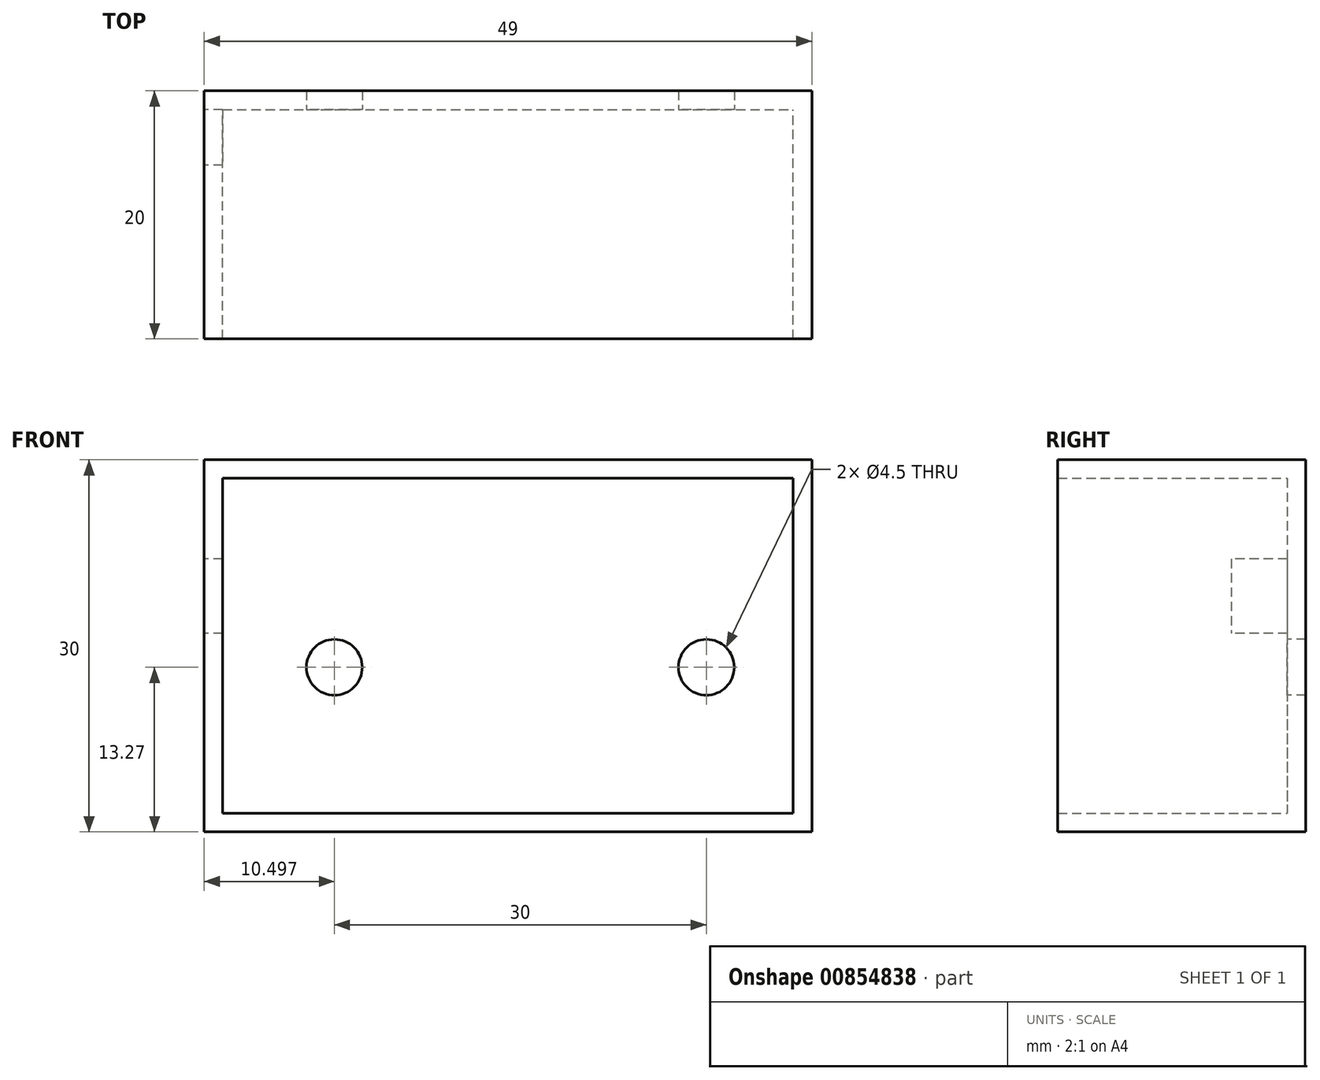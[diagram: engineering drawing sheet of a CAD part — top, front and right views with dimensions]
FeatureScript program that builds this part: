
annotation { "Feature Type Name" : "Feature", "Feature Type Description" : "" }
export const myFeature = defineFeature(function(context is Context, id is Id, definition is map)
    precondition{}
    {
        {
            var Q0;
            Q0=qCreatedBy(makeId("Front.planeOp"),FACE);
            var sketch = newSketch(context, id + "F0", { "sketchPlane" : qUnion([Q0])});
            skLineSegment(sketch, "E0.bottom", {"start": v(-23.27, 16.73) * mm, "end": v(25.73, 16.73) * mm});
            skLineSegment(sketch, "E0.top", {"start": v(-23.27, -13.27) * mm, "end": v(25.73, -13.27) * mm});
            skLineSegment(sketch, "E0.left", {"start": v(-23.27, 16.73) * mm, "end": v(-23.27, -13.27) * mm});
            skLineSegment(sketch, "E0.right", {"start": v(25.73, 16.73) * mm, "end": v(25.73, -13.27) * mm});
            skSolve(sketch);
        }
        {
            var Q0;
            Q0=makeQuery(id+"F0.imprint","IMPRINT",FACE,{"disambiguationData":[TD([[makeQuery(id+"F0.imprint","IMPRINT",EDGE,{"derivedFrom":sQuery(id+"F0.wireOp",EDGE,"E0.bottom")}),-1.0]])]});
            extrude(context, id + "F1", {"entities" : qUnion([Q0]), "depth" : 20 * mm, "offsetDistance" : 25 * mm});
        }
        {
            var Q0;
            Q0=makeQuery(id+"F1.opExtrude","CAP_FACE",FACE,{"disambiguationData":[OSD([sQuery(id+"F0.wireOp",EDGE,"E0.bottom"),sQuery(id+"F0.wireOp",EDGE,"E0.top"),sQuery(id+"F0.wireOp",EDGE,"E0.left"),sQuery(id+"F0.wireOp",EDGE,"E0.right")])],"isStart":false});
            shell(context, id + "F2", {"entities" : qUnion([Q0]), "thickness" : 1.5 * mm});
        }
        {
            var Q0;
            Q0=makeQuery(id+"F2.opShell","OFFSET_FACE",FACE,{"disambiguationData":[OSD([sQuery(id+"F0.wireOp",EDGE,"E0.bottom"),sQuery(id+"F0.wireOp",EDGE,"E0.top"),sQuery(id+"F0.wireOp",EDGE,"E0.left"),sQuery(id+"F0.wireOp",EDGE,"E0.right")])]});
            var sketch = newSketch(context, id + "F3", { "sketchPlane" : qUnion([Q0])});
            skCircle(sketch, "E1", {"center": v(-12.77, 0) * mm, "radius": 2.25 * mm});
            skCircle(sketch, "E2", {"center": v(17.23, 0) * mm, "radius": 2.25 * mm});
            skSolve(sketch);
        }
        {
            var Q0;
            Q0=makeQuery(id+"F3.imprint","IMPRINT",FACE,{"disambiguationData":[TD([[makeQuery(id+"F3.imprint","IMPRINT",EDGE,{"derivedFrom":sQuery(id+"F3.wireOp",EDGE,"E1")}),1.0]])]});
            var Q1;
            Q1=makeQuery(id+"F3.imprint","IMPRINT",FACE,{"disambiguationData":[TD([[makeQuery(id+"F3.imprint","IMPRINT",EDGE,{"derivedFrom":sQuery(id+"F3.wireOp",EDGE,"E2")}),1.0]])]});
            extrude(context, id + "F4", {"entities" : qUnion([Q0, Q1]), "operationType" : NewBodyOperationType.REMOVE, "endBound" : BoundingType.UP_TO_NEXT, "oppositeDirection" : true, "depth" : 25 * mm, "offsetDistance" : 25 * mm});
        }
        {
            var Q0;
            Q0=makeQuery(id+"F1.opExtrude","SWEPT_FACE",FACE,{"disambiguationData":[OSD([sQuery(id+"F0.wireOp",EDGE,"E0.left")])]});
            var sketch = newSketch(context, id + "F5", { "sketchPlane" : qUnion([Q0])});
            skLineSegment(sketch, "E3.bottom", {"start": v(1.5, 8.73) * mm, "end": v(6, 8.73) * mm});
            skLineSegment(sketch, "E3.top", {"start": v(1.5, 2.73) * mm, "end": v(6, 2.73) * mm});
            skLineSegment(sketch, "E3.left", {"start": v(1.5, 8.73) * mm, "end": v(1.5, 2.73) * mm});
            skLineSegment(sketch, "E3.right", {"start": v(6, 8.73) * mm, "end": v(6, 2.73) * mm});
            skSolve(sketch);
        }
        {
            var Q0;
            Q0=makeQuery(id+"F5.imprint","IMPRINT",FACE,{"disambiguationData":[TD([[makeQuery(id+"F5.imprint","IMPRINT",EDGE,{"derivedFrom":sQuery(id+"F5.wireOp",EDGE,"E3.bottom")}),-1.0]])]});
            extrude(context, id + "F6", {"entities" : qUnion([Q0]), "operationType" : NewBodyOperationType.REMOVE, "endBound" : BoundingType.UP_TO_NEXT, "oppositeDirection" : true, "depth" : 25 * mm, "offsetDistance" : 25 * mm});
        }
    });
